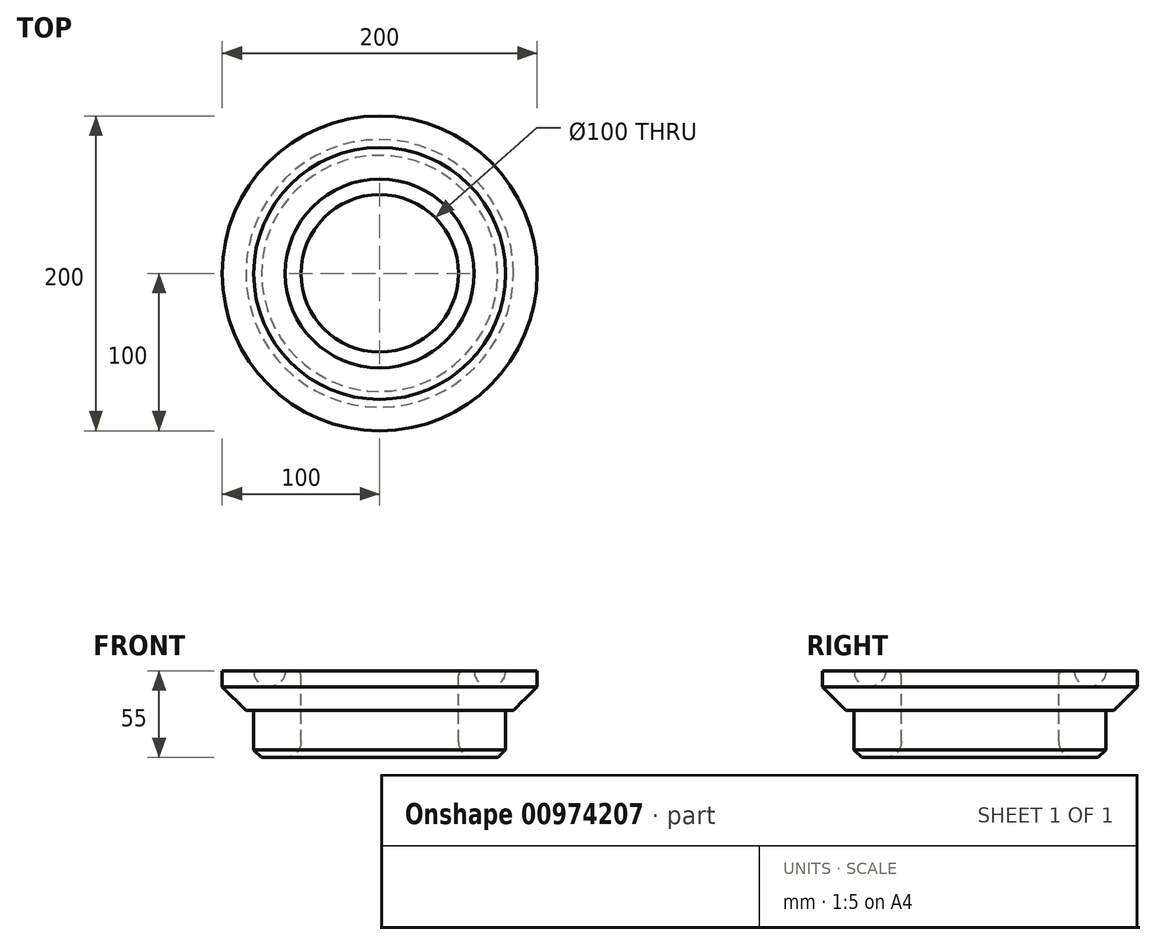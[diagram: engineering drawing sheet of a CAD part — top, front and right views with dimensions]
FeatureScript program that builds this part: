
annotation { "Feature Type Name" : "Feature", "Feature Type Description" : "" }
export const myFeature = defineFeature(function(context is Context, id is Id, definition is map)
    precondition{}
    {
        {
            var Q0;
            Q0=qCreatedBy(makeId("Right.planeOp"),FACE);
            var sketch = newSketch(context, id + "F0", { "sketchPlane" : qUnion([Q0])});
            skLineSegment(sketch, "E0", {"start": v(0, 55.7) * mm, "end": v(0, -149.02) * mm, "construction": true});
            skLineSegment(sketch, "E1", {"start": v(50, 0) * mm, "end": v(50, -55) * mm});
            skLineSegment(sketch, "E2", {"start": v(50, -55) * mm, "end": v(80, -55) * mm});
            skLineSegment(sketch, "E3", {"start": v(80, -55) * mm, "end": v(80, -25) * mm});
            skLineSegment(sketch, "E4", {"start": v(80, -25) * mm, "end": v(85, -25) * mm});
            skLineSegment(sketch, "E5", {"start": v(85, -25) * mm, "end": v(100, -10) * mm});
            skLineSegment(sketch, "E6", {"start": v(100, -10) * mm, "end": v(100, 0) * mm});
            skLineSegment(sketch, "E7", {"start": v(50, 0) * mm, "end": v(60, 0) * mm});
            skArc(sketch, "E8", {"start": v(60, 0) * mm, "mid": v(70, -10) * mm, "end": v(80, 0) * mm});
            skLineSegment(sketch, "E9", {"start": v(100, 0) * mm, "end": v(80, 0) * mm});
            skSolve(sketch);
        }
        {
            var Q0;
            Q0=makeQuery(id+"F0.imprint","IMPRINT",FACE,{"disambiguationData":[TD([[makeQuery(id+"F0.imprint","IMPRINT",EDGE,{"derivedFrom":sQuery(id+"F0.wireOp",EDGE,"E1")}),1.0]])]});
            var Q1;
            Q1=sQuery(id+"F0.wireOp",EDGE,"E0");
            revolve(context, id + "F1", {"surfaceOperationType" : NewSurfaceOperationType.NEW, "entities" : qUnion([Q0]), "axis" : qUnion([Q1]), "revolveType" : RevolveType.FULL});
        }
        {
            var Q0;
            Q0=makeQuery(id+"F1.opRevolve","SWEPT_EDGE",EDGE,{"disambiguationData":[OSD([sQuery(id+"F0.wireOp",EDGE,"E2"),sQuery(id+"F0.wireOp",EDGE,"E3")])]});
            chamfer(context, id + "F2", {"entities" : qUnion([Q0]), "width" : 5 * mm, "tangentPropagation" : true});
        }
        {
            var Q0;
            Q0=makeQuery(id+"F1.opRevolve","SWEPT_EDGE",EDGE,{"disambiguationData":[OSD([sQuery(id+"F0.wireOp",EDGE,"E1"),sQuery(id+"F0.wireOp",EDGE,"E2")])]});
            fillet(context, id + "F3", {"entities" : qUnion([Q0]), "radius" : 10 * mm, "tangentPropagation" : true, "allowEdgeOverflow" : false});
        }
        {
            var Q0;
            Q0=makeQuery(id+"F1.opRevolve","SWEPT_EDGE",EDGE,{"disambiguationData":[OSD([sQuery(id+"F0.wireOp",EDGE,"E1"),sQuery(id+"F0.wireOp",EDGE,"E7")])]});
            fillet(context, id + "F4", {"entities" : qUnion([Q0]), "radius" : 3 * mm, "tangentPropagation" : true, "allowEdgeOverflow" : false});
        }
    });
